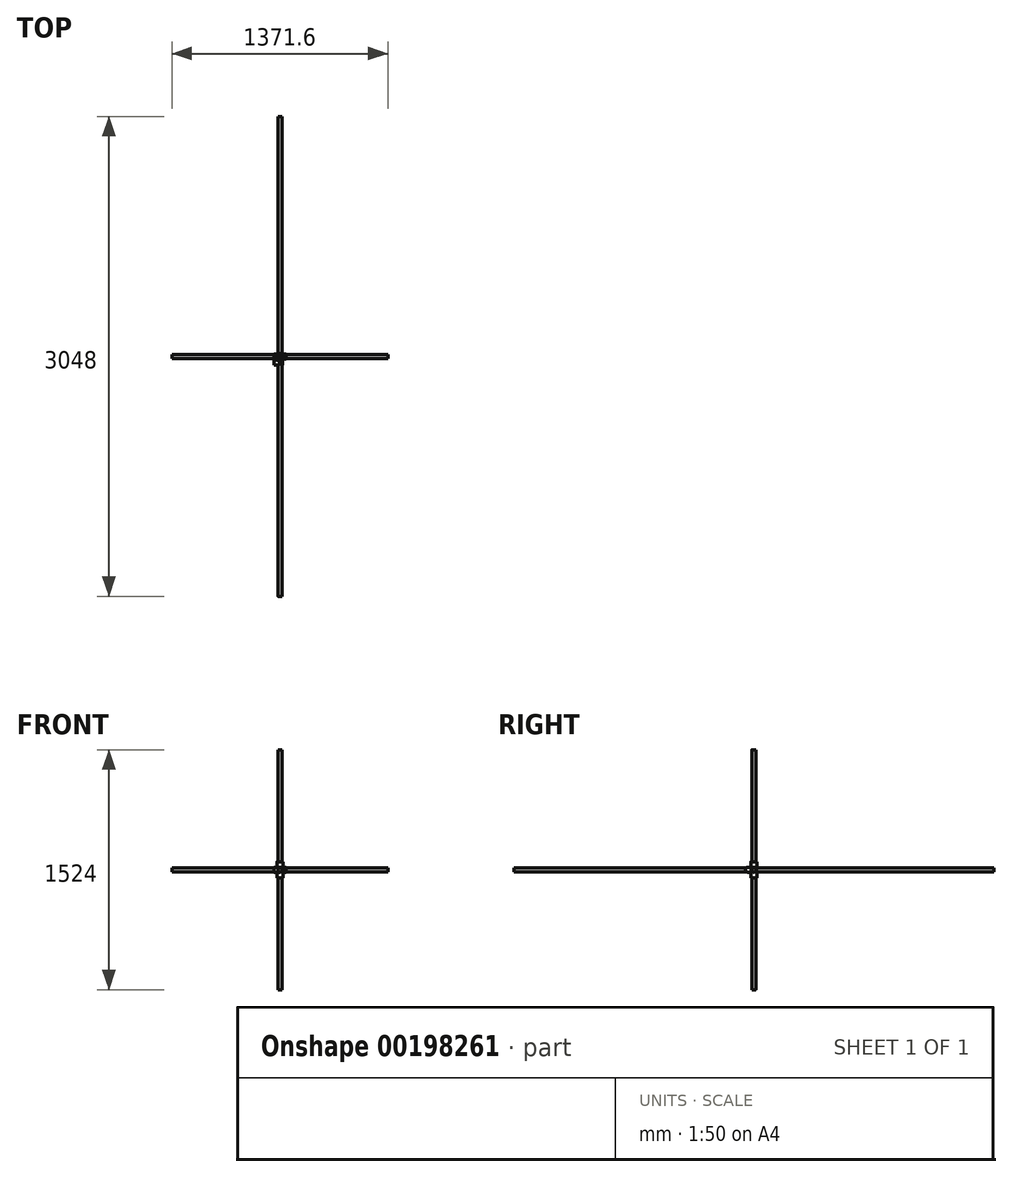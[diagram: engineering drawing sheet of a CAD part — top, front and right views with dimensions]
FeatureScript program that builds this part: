
annotation { "Feature Type Name" : "Feature", "Feature Type Description" : "" }
export const myFeature = defineFeature(function(context is Context, id is Id, definition is map)
    precondition{}
    {
        {
            var Q0;
            Q0=qCreatedBy(makeId("Front.planeOp"),FACE);
            var sketch = newSketch(context, id + "F0", { "sketchPlane" : qUnion([Q0])});
            skCircle(sketch, "E0", {"center": v(0, 0) * mm, "radius": 12.7 * mm});
            skSolve(sketch);
        }
        {
            var Q0;
            Q0 = qSketchRegion(id + "F0", true);
            extrude(context, id + "F1", {"entities" : qUnion([Q0]), "depth" : 3048 * mm, "symmetric" : true});
        }
        {
            var Q0;
            Q0=qCreatedBy(makeId("Top.planeOp"),FACE);
            var sketch = newSketch(context, id + "F2", { "sketchPlane" : qUnion([Q0])});
            skLineSegment(sketch, "E1", {"start": v(0, 0) * mm, "end": v(0, -38.1) * mm});
            skLineSegment(sketch, "E2", {"start": v(0, -38.1) * mm, "end": v(-38.1, -38.1) * mm});
            skSolve(sketch);
        }
        {
            var Q0;
            Q0=qCreatedBy(makeId("Front.planeOp"),FACE);
            var sketch = newSketch(context, id + "F3", { "sketchPlane" : qUnion([Q0])});
            skCircle(sketch, "E3", {"center": v(0, 0) * mm, "radius": 15.88 * mm});
            skSolve(sketch);
        }
        {
            var Q0;
            Q0 = qSketchRegion(id + "F3", true);
            var Q1;
            Q1=sQuery(id+"F3.wireOp",EDGE,"E3");
            var Q2;
            Q2 = qConstructionFilter(qBodyType(qCreatedBy(id + "F2" ,EDGE), BodyType.WIRE), ConstructionObject.NO);
            sweep(context, id + "F4", {"profiles" : qUnion([Q0]), "surfaceProfiles" : qUnion([Q1]), "path" : qUnion([Q2])});
        }
        {
            var Q0;
            Q0=qCreatedBy(makeId("Top.planeOp"),FACE);
            var sketch = newSketch(context, id + "F5", { "sketchPlane" : qUnion([Q0])});
            skCircle(sketch, "E4", {"center": v(0, 0) * mm, "radius": 12.7 * mm});
            skSolve(sketch);
        }
        {
            var Q0;
            Q0 = qSketchRegion(id + "F5", true);
            extrude(context, id + "F6", {"entities" : qUnion([Q0]), "depth" : 1524 * mm, "symmetric" : true});
        }
        {
            var Q0;
            Q0=qCreatedBy(makeId("Right.planeOp"),FACE);
            var sketch = newSketch(context, id + "F7", { "sketchPlane" : qUnion([Q0])});
            skCircle(sketch, "E5", {"center": v(0, 0) * mm, "radius": 15.88 * mm});
            skSolve(sketch);
        }
        {
            var Q0;
            Q0 = qSketchRegion(id + "F7", true);
            extrude(context, id + "F8", {"entities" : qUnion([Q0]), "depth" : 76.2 * mm, "symmetric" : true});
        }
        {
            var Q0;
            Q0=qCreatedBy(makeId("Top.planeOp"),FACE);
            var sketch = newSketch(context, id + "F9", { "sketchPlane" : qUnion([Q0])});
            skCircle(sketch, "E6", {"center": v(0, 0) * mm, "radius": 15.88 * mm});
            skSolve(sketch);
        }
        {
            var Q0;
            Q0 = qSketchRegion(id + "F9", true);
            extrude(context, id + "F10", {"entities" : qUnion([Q0]), "operationType" : NewBodyOperationType.ADD, "depth" : 38.1 * mm});
        }
        {
            var Q0;
            Q0=qCreatedBy(makeId("Top.planeOp"),FACE);
            var sketch = newSketch(context, id + "F11", { "sketchPlane" : qUnion([Q0])});
            skCircle(sketch, "E7", {"center": v(0, 0) * mm, "radius": 19.05 * mm});
            skSolve(sketch);
        }
        {
            var Q0;
            Q0 = qSketchRegion(id + "F11", true);
            extrude(context, id + "F12", {"entities" : qUnion([Q0]), "depth" : 101.6 * mm, "symmetric" : true});
        }
        {
            var Q0;
            Q0=qCreatedBy(makeId("Front.planeOp"),FACE);
            var sketch = newSketch(context, id + "F13", { "sketchPlane" : qUnion([Q0])});
            skCircle(sketch, "E8", {"center": v(0, 0) * mm, "radius": 15.88 * mm});
            skSolve(sketch);
        }
        {
            var Q0;
            Q0 = qSketchRegion(id + "F13", true);
            extrude(context, id + "F14", {"entities" : qUnion([Q0]), "operationType" : NewBodyOperationType.ADD, "depth" : 38.1 * mm});
        }
        {
            var Q0;
            Q0=qCreatedBy(makeId("Right.planeOp"),FACE);
            var sketch = newSketch(context, id + "F15", { "sketchPlane" : qUnion([Q0])});
            skCircle(sketch, "E9", {"center": v(0, 0) * mm, "radius": 12.7 * mm});
            skSolve(sketch);
        }
        {
            var Q0;
            Q0 = qSketchRegion(id + "F15", true);
            extrude(context, id + "F16", {"entities" : qUnion([Q0]), "depth" : 1371.6 * mm, "symmetric" : true});
        }
    });
